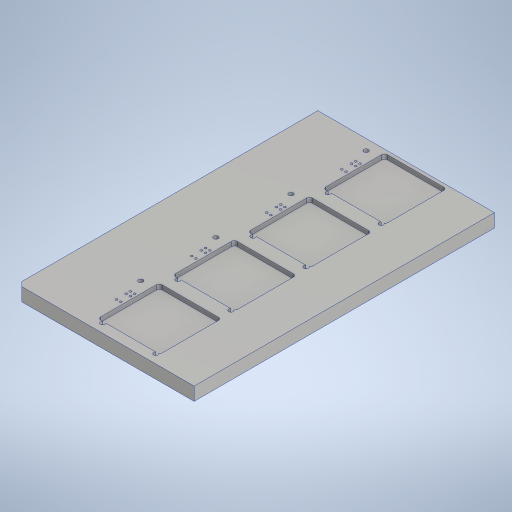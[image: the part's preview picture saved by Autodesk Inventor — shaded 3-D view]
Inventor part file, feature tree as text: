
AUTODESK INVENTOR PART (.ipt)
format: ipt  version: 2023 (Build 270158000, 158)  size: 405,504 bytes
history: native  units: in
note: dims shown in document units (in); Inventor stores cm internally (conversion verified against a paired STEP export)
features: sketch x4, extrude x3, chamfer x1, hole x1
ambient origin geometry x8: Origin, YZ Plane, XZ Plane, XY Plane, X Axis, Y Axis, Z Axis, Center Point
bodies: Solid1 (feature_tree)
feature tree (9):
  extrude  "Extrusion1"  Depth=8.5in
  chamfer  "Chamfer1"  Distance=0.375in
  extrude  "Extrusion10"  Depth=0.125in
  extrude  "Extrusion11"  Depth=0.5in
  hole  "Hole3"  [1 undecoded]
  sketch  "Sketch1"  dims[d0=5.0in d1=8.5in d2=0.375in d3=0.0in]
  sketch  "Sketch12"  dims[d126=0.125in d127=0.125in d128=45.0deg d166=0.125in]
  sketch  "Sketch13"  dims[d167=1.5in d169=0.5in]
  sketch  "Sketch14"  dims[d170=1.5748in d171=1.0in d172=0.0in d194=1.5748in d196=2.125in d197=0.3937in d199=1.0in d221=0.125in d222=0.0in d241=1.752in d242=1.7362in d243=0.0787in d244=1.5748in d246=2.125in d247=0.3937in d249=0.3937in d252=0.0428in d253=0.125in d254=2.1654in d255=0.25in d256=0.125in d257=0.3184in d259=0.2756in d261=0.0591in d262=0.2362in d263=0.146in d264=0.0787in d265=0.5635in d266=0.315in d267=0.8108in d269=0.1181in d278=0.0886in d279=0.7753in d280=0.1181in d281=1.5748in d283=2.125in d284=0.3937in d286=0.3937in]
note: 1 required parameter value undecoded (feature->parameter linkage not recoverable at this tier; creation-order binding heuristic only, values carry confidence <= 0.55)
